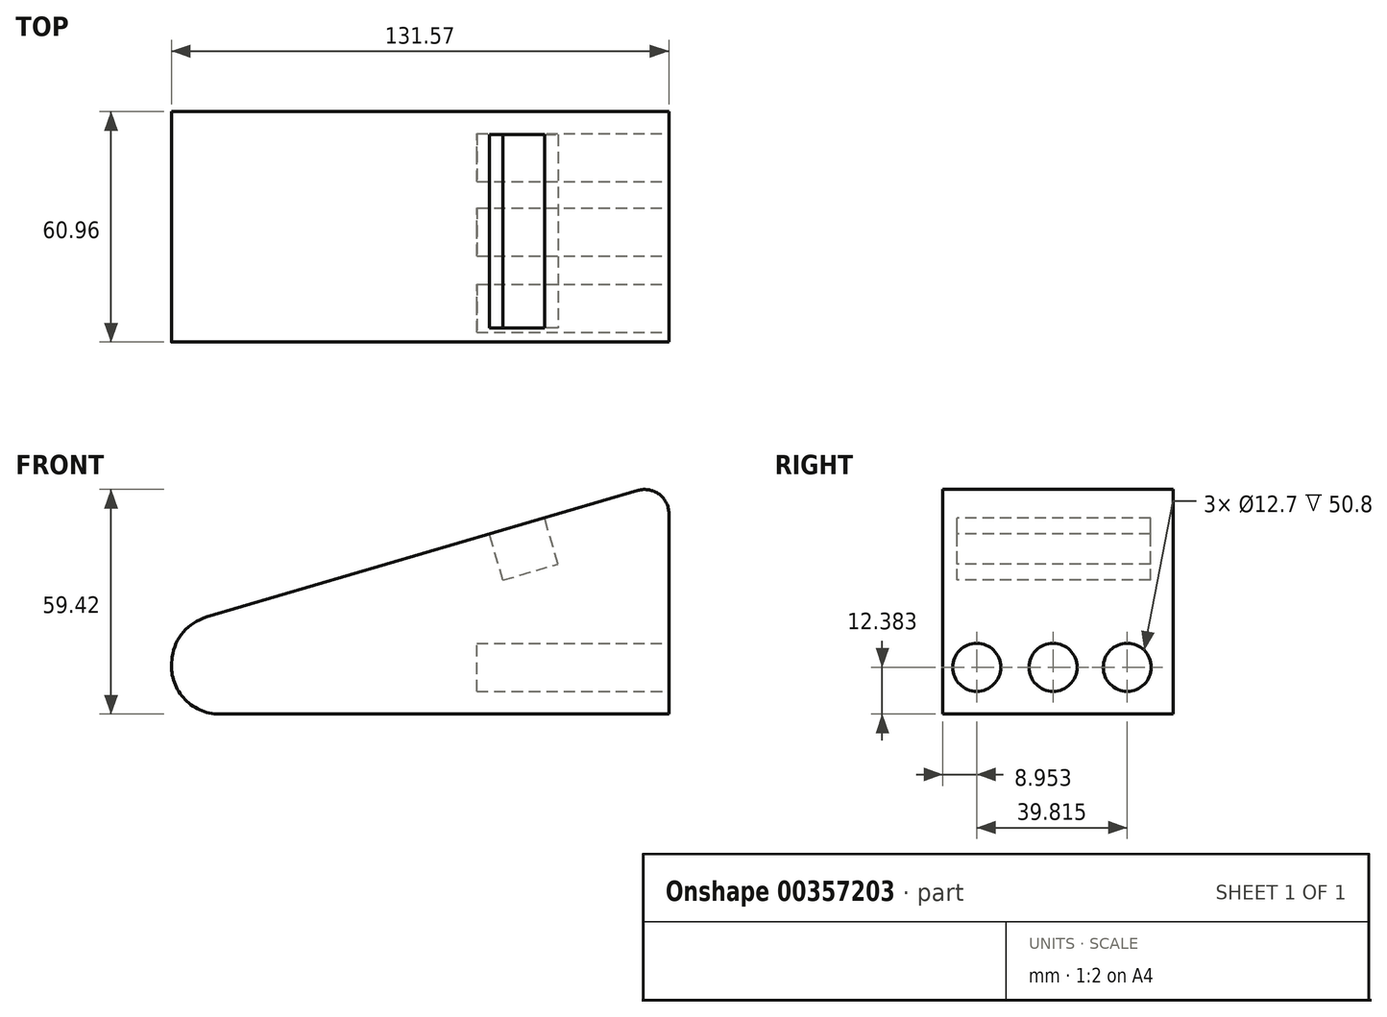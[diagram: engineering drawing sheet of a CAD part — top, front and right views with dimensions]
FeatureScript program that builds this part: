
annotation { "Feature Type Name" : "Feature", "Feature Type Description" : "" }
export const myFeature = defineFeature(function(context is Context, id is Id, definition is map)
    precondition{}
    {
        {
            var Q0;
            Q0=qCreatedBy(makeId("Front.planeOp"),FACE);
            var sketch = newSketch(context, id + "F0", { "sketchPlane" : qUnion([Q0])});
            skLineSegment(sketch, "E0", {"start": v(-68.03, 0) * mm, "end": v(65.33, 0) * mm});
            skLineSegment(sketch, "E1", {"start": v(65.33, 0) * mm, "end": v(65.33, 53.07) * mm});
            skLineSegment(sketch, "E2", {"start": v(57.19, 59.16) * mm, "end": v(-57.02, 25.63) * mm});
            skLineSegment(sketch, "E3", {"start": v(-66.03, 15.1) * mm, "end": v(-68.03, 0) * mm});
            skPoint(sketch, "E4.visualSharp", {"position": v(-64.95, 23.3) * mm});
            skArc(sketch, "E4.filletArc", {"start": v(-57.02, 25.63) * mm, "mid": v(-63.09, 21.7) * mm, "end": v(-66.03, 15.1) * mm});
            skPoint(sketch, "E5.visualSharp", {"position": v(65.33, 61.55) * mm});
            skArc(sketch, "E5.filletArc", {"start": v(65.33, 53.07) * mm, "mid": v(62.78, 58.15) * mm, "end": v(57.19, 59.16) * mm});
            skSolve(sketch);
        }
        {
            var Q0;
            Q0=makeQuery(id+"F0.imprint","IMPRINT",FACE,{"disambiguationData":[TD([[makeQuery(id+"F0.imprint","IMPRINT",EDGE,{"derivedFrom":sQuery(id+"F0.wireOp",EDGE,"E0")}),1.0]])]});
            extrude(context, id + "F1", {"entities" : qUnion([Q0]), "depth" : 60.96 * mm});
        }
        {
            var Q0;
            Q0=makeQuery(id+"F1.opExtrude","SWEPT_FACE",FACE,{"disambiguationData":[OSD([sQuery(id+"F0.wireOp",EDGE,"E2")])]});
            var sketch = newSketch(context, id + "F2", { "sketchPlane" : qUnion([Q0])});
            skLineSegment(sketch, "E6.bottom", {"start": v(30.56, -6.08) * mm, "end": v(45.74, -6.08) * mm});
            skLineSegment(sketch, "E6.top", {"start": v(30.56, -57.17) * mm, "end": v(45.74, -57.17) * mm});
            skLineSegment(sketch, "E6.left", {"start": v(30.56, -6.08) * mm, "end": v(30.56, -57.17) * mm});
            skLineSegment(sketch, "E6.right", {"start": v(45.74, -6.08) * mm, "end": v(45.74, -57.17) * mm});
            skSolve(sketch);
        }
        {
            var Q0;
            Q0 = qSketchRegion(id + "F2", true);
            extrude(context, id + "F3", {"entities" : qUnion([Q0]), "operationType" : NewBodyOperationType.REMOVE, "oppositeDirection" : true, "depth" : 12.7 * mm});
        }
        {
            var Q0;
            Q0=makeQuery(id+"F1.opExtrude","SWEPT_EDGE",EDGE,{"disambiguationData":[OSD([sQuery(id+"F0.wireOp",EDGE,"E0"),sQuery(id+"F0.wireOp",EDGE,"E3")])]});
            fillet(context, id + "F4", {"entities" : qUnion([Q0]), "radius" : 12.7 * mm, "tangentPropagation" : true, "allowEdgeOverflow" : false});
        }
        {
            var Q0;
            Q0=makeQuery(id+"F1.opExtrude","SWEPT_FACE",FACE,{"disambiguationData":[OSD([sQuery(id+"F0.wireOp",EDGE,"E1")])]});
            var sketch = newSketch(context, id + "F5", { "sketchPlane" : qUnion([Q0])});
            skCircle(sketch, "E7", {"center": v(-52, 12.38) * mm, "radius": 6.35 * mm});
            skCircle(sketch, "E8", {"center": v(-31.81, 12.38) * mm, "radius": 6.35 * mm});
            skCircle(sketch, "E9", {"center": v(-12.2, 12.38) * mm, "radius": 6.35 * mm});
            skSolve(sketch);
        }
        {
            var Q0;
            Q0 = qSketchRegion(id + "F5", true);
            extrude(context, id + "F6", {"entities" : qUnion([Q0]), "operationType" : NewBodyOperationType.REMOVE, "oppositeDirection" : true, "depth" : 50.8 * mm});
        }
    });
